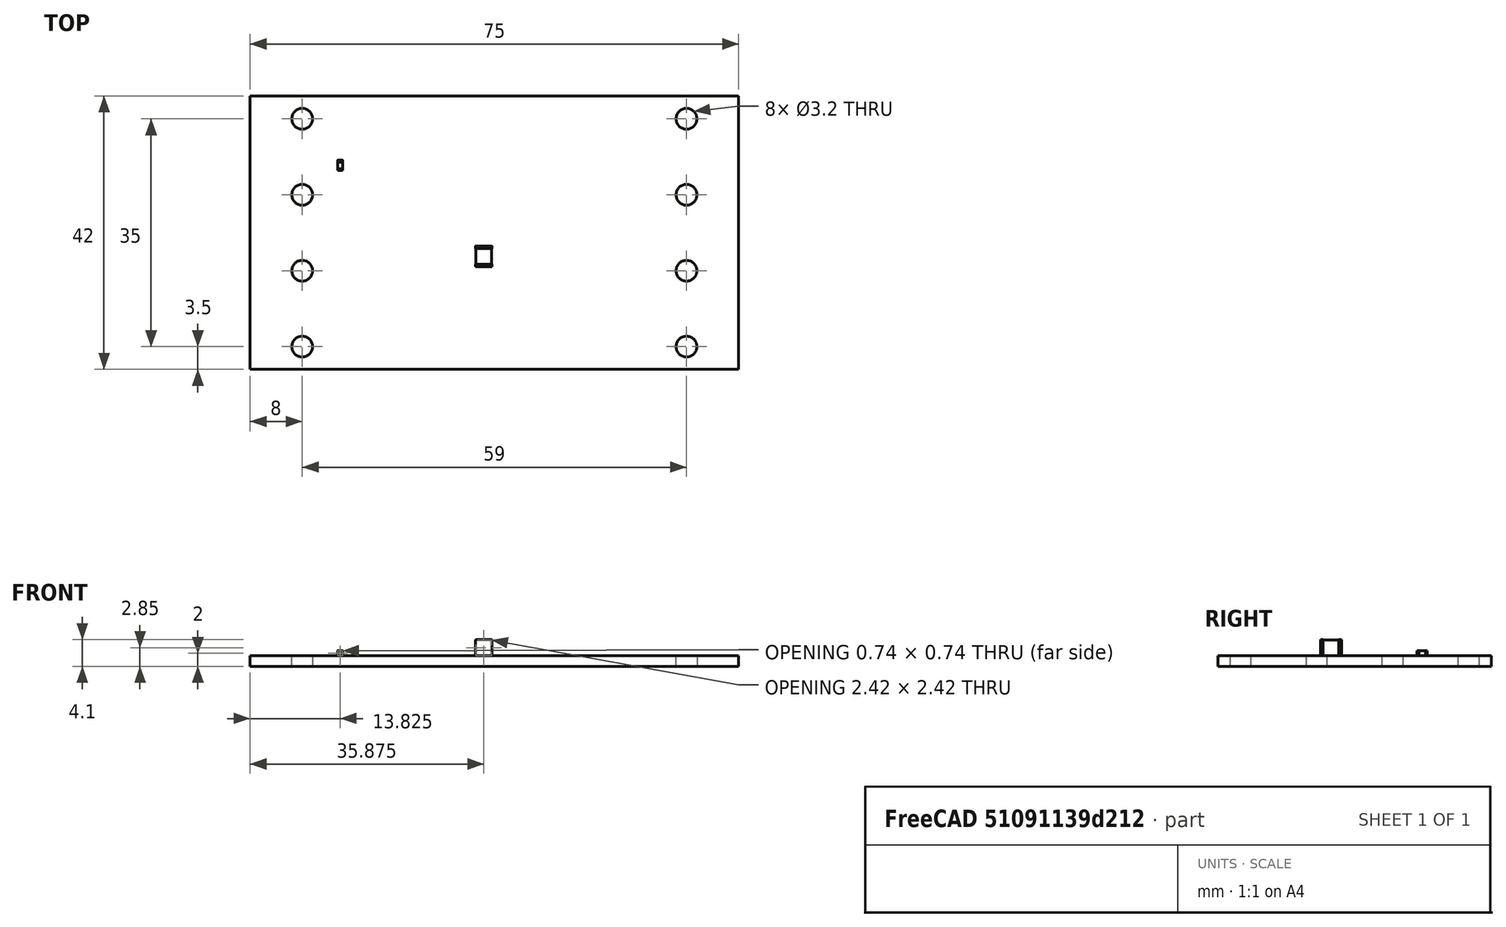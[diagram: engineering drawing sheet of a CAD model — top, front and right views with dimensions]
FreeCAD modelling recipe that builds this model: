
FCSTD DOCUMENT  (FreeCAD 0.19R24291 (Git))
Label: caps
License: Creative Commons Attribution-NonCommercial-ShareAlike
LicenseURL: http://creativecommons.org/licenses/by-nc-sa/4.0/
objects: App::Link×106, PartDesign::Line×8, App::LinkGroup×4, Part::Feature×3, PartDesign::CoordinateSystem×2, Sketcher::SketchObject×1, App::Part×1
note: 14 computed .brp shape members not serialized (recipe doc carries the construction recipe); baked Part::Feature solids carry a one-line shape summary decoded from their .brp

FEATURE [PartDesign::CoordinateSystem] Local_CS_1fb6
  AttacherType = Attacher::AttachEngine3D
FEATURE [Part::Feature] Pcb_1fb6
  Placement = pos=(-110.5,80.5,0) rot=(0,0,1;0rad)
  shape: bbox 75 x 42 x 1.6 mm, 14 faces (baked)
FEATURE [Sketcher::SketchObject] PCB_Sketch_1fb6
  FullyConstrained = false
  sketch-geometry (4):
    g0: LineSegment StartX=0 StartY=0 StartZ=0 EndX=75 EndY=0 EndZ=0
    g1: LineSegment StartX=0 StartY=-42 StartZ=0 EndX=0 EndY=0 EndZ=0
    g2: LineSegment StartX=75 StartY=-42 StartZ=0 EndX=0 EndY=-42 EndZ=0
    g3: LineSegment StartX=75 StartY=0 StartZ=0 EndX=75 EndY=-42 EndZ=0
  constraints (4):
    c: Coincident(g1,g2)
    c: Coincident(g0,g1)
    c: Coincident(g2,g3)
    c: Coincident(g0,g3)
FEATURE [App::LinkGroup] Board_Geoms_1fb6
  ElementList = -> [Pcb_1fb6,Local_CS_1fb6,PCB_Sketch_1fb6]
  LinkMode = 0
FEATURE [Part::Feature] Shape  label="C232_C_0603_1608Metric_6077F2BE"
  Placement = pos=(13.825,-10.655,0) rot=(0,0,-1;1.5708rad)
  shape: bbox 0.8 x 1.6 x 0.8 mm, 28 faces (baked)
FEATURE [App::Link] C232_C_0603_1608Metric_6077F2BE_ln_  label="C231_C_0603_1608Metric_607530A9"
  LinkPlacement = pos=(12.3,-10.65,0) rot=(0,0,-1;1.5708rad)
  LinkedObject = -> Shape
  Placement = pos=(12.3,-10.65,0) rot=(0,0,-1;1.5708rad)
FEATURE [Part::Feature] Shape001  label="C230_C_1210_3225Metric_6077E91F"
  Placement = pos=(35.875,-24.645,0) rot=(0,0,-1;1.5708rad)
  shape: bbox 2.5 x 3.2 x 2.5 mm, 28 faces (baked)
FEATURE [App::Link] C230_C_1210_3225Metric_6077E91F_ln_  label="C229_C_1210_3225Metric_6077F675"
  LinkPlacement = pos=(19.575,-10.655,0) rot=(0,0,-1;1.5708rad)
  LinkedObject = -> Shape001
  Placement = pos=(19.575,-10.655,0) rot=(0,0,-1;1.5708rad)
FEATURE [App::Link] C230_C_1210_3225Metric_6077E91F_ln_001  label="C228_C_1210_3225Metric_6077E3C7"
  LinkPlacement = pos=(32.625,-24.645,0) rot=(0,0,-1;1.5708rad)
  LinkedObject = -> Shape001
  Placement = pos=(32.625,-24.645,0) rot=(0,0,-1;1.5708rad)
FEATURE [App::Link] C230_C_1210_3225Metric_6077E91F_ln_002  label="C227_C_1210_3225Metric_6077FA4A"
  LinkPlacement = pos=(32.575,-10.655,0) rot=(0,0,-1;1.5708rad)
  LinkedObject = -> Shape001
  Placement = pos=(32.575,-10.655,0) rot=(0,0,-1;1.5708rad)
FEATURE [App::Link] C230_C_1210_3225Metric_6077E91F_ln_003  label="C225_C_1210_3225Metric_6077EF6A"
  LinkPlacement = pos=(26.075,-10.655,0) rot=(0,0,-1;1.5708rad)
  LinkedObject = -> Shape001
  Placement = pos=(26.075,-10.655,0) rot=(0,0,-1;1.5708rad)
FEATURE [App::Link] C230_C_1210_3225Metric_6077E91F_ln_004  label="C222_C_1210_3225Metric_6077F4A1"
  LinkPlacement = pos=(26.125,-24.645,0) rot=(0,0,-1;1.5708rad)
  LinkedObject = -> Shape001
  Placement = pos=(26.125,-24.645,0) rot=(0,0,-1;1.5708rad)
FEATURE [App::Link] C230_C_1210_3225Metric_6077E91F_ln_005  label="C221_C_1210_3225Metric_6077EDA8"
  LinkPlacement = pos=(42.325,-10.655,0) rot=(0,0,-1;1.5708rad)
  LinkedObject = -> Shape001
  Placement = pos=(42.325,-10.655,0) rot=(0,0,-1;1.5708rad)
FEATURE [App::Link] C230_C_1210_3225Metric_6077E91F_ln_006  label="C218_C_1210_3225Metric_6077F705"
  LinkPlacement = pos=(16.375,-24.65,0) rot=(0,0,-1;1.5708rad)
  LinkedObject = -> Shape001
  Placement = pos=(16.375,-24.65,0) rot=(0,0,-1;1.5708rad)
FEATURE [App::Link] C230_C_1210_3225Metric_6077E91F_ln_007  label="C217_C_1210_3225Metric_6077EF34"
  LinkPlacement = pos=(16.375,-10.65,0) rot=(0,0,-1;1.5708rad)
  LinkedObject = -> Shape001
  Placement = pos=(16.375,-10.65,0) rot=(0,0,-1;1.5708rad)
FEATURE [App::Link] C230_C_1210_3225Metric_6077E91F_ln_008  label="C216_C_1210_3225Metric_6077F9F0"
  LinkPlacement = pos=(35.825,-10.655,0) rot=(0,0,-1;1.5708rad)
  LinkedObject = -> Shape001
  Placement = pos=(35.825,-10.655,0) rot=(0,0,-1;1.5708rad)
FEATURE [App::Link] C230_C_1210_3225Metric_6077E91F_ln_009  label="C215_C_1210_3225Metric_6077E9EE"
  LinkPlacement = pos=(39.075,-10.655,0) rot=(0,0,-1;1.5708rad)
  LinkedObject = -> Shape001
  Placement = pos=(39.075,-10.655,0) rot=(0,0,-1;1.5708rad)
FEATURE [App::Link] C230_C_1210_3225Metric_6077E91F_ln_010  label="C214_C_1210_3225Metric_6077F0CC"
  LinkPlacement = pos=(19.625,-24.645,0) rot=(0,0,-1;1.5708rad)
  LinkedObject = -> Shape001
  Placement = pos=(19.625,-24.645,0) rot=(0,0,-1;1.5708rad)
FEATURE [App::Link] C230_C_1210_3225Metric_6077E91F_ln_011  label="C213_C_1210_3225Metric_6077EB6E"
  LinkPlacement = pos=(45.625,-24.645,0) rot=(0,0,-1;1.5708rad)
  LinkedObject = -> Shape001
  Placement = pos=(45.625,-24.645,0) rot=(0,0,-1;1.5708rad)
FEATURE [App::Link] C232_C_0603_1608Metric_6077F2BE_ln_001  label="C212_C_0603_1608Metric_6077F138"
  LinkPlacement = pos=(62.625,-24.6325,0) rot=(0,0,-1;1.5708rad)
  LinkedObject = -> Shape
  Placement = pos=(62.625,-24.6325,0) rot=(0,0,-1;1.5708rad)
FEATURE [App::Link] C232_C_0603_1608Metric_6077F2BE_ln_002  label="C211_C_0603_1608Metric_6077E469"
  LinkPlacement = pos=(61.075,-10.655,0) rot=(0,0,-1;1.5708rad)
  LinkedObject = -> Shape
  Placement = pos=(61.075,-10.655,0) rot=(0,0,-1;1.5708rad)
FEATURE [App::Link] C232_C_0603_1608Metric_6077F2BE_ln_003  label="C210_C_0603_1608Metric_6077F9C0"
  LinkPlacement = pos=(12.375,-24.645,0) rot=(0,0,-1;1.5708rad)
  LinkedObject = -> Shape
  Placement = pos=(12.375,-24.645,0) rot=(0,0,-1;1.5708rad)
FEATURE [App::Link] C232_C_0603_1608Metric_6077F2BE_ln_004  label="C209_C_0603_1608Metric_6077E2A4"
  LinkPlacement = pos=(62.575,-10.655,0) rot=(0,0,-1;1.5708rad)
  LinkedObject = -> Shape
  Placement = pos=(62.575,-10.655,0) rot=(0,0,-1;1.5708rad)
FEATURE [App::Link] C230_C_1210_3225Metric_6077E91F_ln_012  label="C208_C_1210_3225Metric_6077F1FE"
  LinkPlacement = pos=(52.075,-10.655,0) rot=(0,0,-1;1.5708rad)
  LinkedObject = -> Shape001
  Placement = pos=(52.075,-10.655,0) rot=(0,0,-1;1.5708rad)
FEATURE [App::Link] C230_C_1210_3225Metric_6077E91F_ln_013  label="C207_C_1210_3225Metric_6077EAE7"
  LinkPlacement = pos=(55.375,-24.645,0) rot=(0,0,-1;1.5708rad)
  LinkedObject = -> Shape001
  Placement = pos=(55.375,-24.645,0) rot=(0,0,-1;1.5708rad)
FEATURE [App::Link] C230_C_1210_3225Metric_6077E91F_ln_014  label="C206_C_1210_3225Metric_6077E7AE"
  LinkPlacement = pos=(48.875,-24.645,0) rot=(0,0,-1;1.5708rad)
  LinkedObject = -> Shape001
  Placement = pos=(48.875,-24.645,0) rot=(0,0,-1;1.5708rad)
FEATURE [App::Link] C230_C_1210_3225Metric_6077E91F_ln_015  label="C204_C_1210_3225Metric_6077EC8B"
  LinkPlacement = pos=(45.575,-10.655,0) rot=(0,0,-1;1.5708rad)
  LinkedObject = -> Shape001
  Placement = pos=(45.575,-10.655,0) rot=(0,0,-1;1.5708rad)
FEATURE [App::Link] C230_C_1210_3225Metric_6077E91F_ln_016  label="C203_C_1210_3225Metric_6077EC58"
  LinkPlacement = pos=(22.875,-24.645,0) rot=(0,0,-1;1.5708rad)
  LinkedObject = -> Shape001
  Placement = pos=(22.875,-24.645,0) rot=(0,0,-1;1.5708rad)
FEATURE [App::Link] C230_C_1210_3225Metric_6077E91F_ln_017  label="C201_C_1210_3225Metric_6077EA1E"
  LinkPlacement = pos=(48.825,-10.655,0) rot=(0,0,-1;1.5708rad)
  LinkedObject = -> Shape001
  Placement = pos=(48.825,-10.655,0) rot=(0,0,-1;1.5708rad)
FEATURE [App::Link] C230_C_1210_3225Metric_6077E91F_ln_018  label="C200_C_1210_3225Metric_6077FC45"
  LinkPlacement = pos=(52.125,-24.645,0) rot=(0,0,-1;1.5708rad)
  LinkedObject = -> Shape001
  Placement = pos=(52.125,-24.645,0) rot=(0,0,-1;1.5708rad)
FEATURE [App::Link] C230_C_1210_3225Metric_6077E91F_ln_019  label="C199_C_1210_3225Metric_6077EAB1"
  LinkPlacement = pos=(55.325,-10.655,0) rot=(0,0,-1;1.5708rad)
  LinkedObject = -> Shape001
  Placement = pos=(55.325,-10.655,0) rot=(0,0,-1;1.5708rad)
FEATURE [App::Link] C230_C_1210_3225Metric_6077E91F_ln_020  label="C198_C_1210_3225Metric_6077F34E"
  LinkPlacement = pos=(29.375,-24.645,0) rot=(0,0,-1;1.5708rad)
  LinkedObject = -> Shape001
  Placement = pos=(29.375,-24.645,0) rot=(0,0,-1;1.5708rad)
FEATURE [App::Link] C230_C_1210_3225Metric_6077E91F_ln_021  label="C196_C_1210_3225Metric_6077EDE1"
  LinkPlacement = pos=(58.625,-24.645,0) rot=(0,0,-1;1.5708rad)
  LinkedObject = -> Shape001
  Placement = pos=(58.625,-24.645,0) rot=(0,0,-1;1.5708rad)
FEATURE [App::Link] C230_C_1210_3225Metric_6077E91F_ln_022  label="C195_C_1210_3225Metric_6077E23E"
  LinkPlacement = pos=(58.575,-10.655,0) rot=(0,0,-1;1.5708rad)
  LinkedObject = -> Shape001
  Placement = pos=(58.575,-10.655,0) rot=(0,0,-1;1.5708rad)
FEATURE [App::Link] C230_C_1210_3225Metric_6077E91F_ln_023  label="C194_C_1210_3225Metric_6077FB79"
  LinkPlacement = pos=(22.825,-10.655,0) rot=(0,0,-1;1.5708rad)
  LinkedObject = -> Shape001
  Placement = pos=(22.825,-10.655,0) rot=(0,0,-1;1.5708rad)
FEATURE [App::Link] C230_C_1210_3225Metric_6077E91F_ln_024  label="C193_C_1210_3225Metric_6077EA7B"
  LinkPlacement = pos=(39.125,-24.645,0) rot=(0,0,-1;1.5708rad)
  LinkedObject = -> Shape001
  Placement = pos=(39.125,-24.645,0) rot=(0,0,-1;1.5708rad)
FEATURE [App::Link] C230_C_1210_3225Metric_6077E91F_ln_025  label="C192_C_1210_3225Metric_6077E5B9"
  LinkPlacement = pos=(42.375,-24.645,0) rot=(0,0,-1;1.5708rad)
  LinkedObject = -> Shape001
  Placement = pos=(42.375,-24.645,0) rot=(0,0,-1;1.5708rad)
FEATURE [App::Link] C230_C_1210_3225Metric_6077E91F_ln_026  label="C191_C_1210_3225Metric_6077E5E9"
  LinkPlacement = pos=(29.325,-10.655,0) rot=(0,0,-1;1.5708rad)
  LinkedObject = -> Shape001
  Placement = pos=(29.325,-10.655,0) rot=(0,0,-1;1.5708rad)
FEATURE [App::Link] C232_C_0603_1608Metric_6077F2BE_ln_005  label="C190_C_0603_1608Metric_6077F465"
  LinkPlacement = pos=(13.875,-24.645,0) rot=(0,0,-1;1.5708rad)
  LinkedObject = -> Shape
  Placement = pos=(13.875,-24.645,0) rot=(0,0,-1;1.5708rad)
FEATURE [App::Link] C232_C_0603_1608Metric_6077F2BE_ln_006  label="C189_C_0603_1608Metric_6077F633"
  LinkPlacement = pos=(61.125,-24.6325,0) rot=(0,0,-1;1.5708rad)
  LinkedObject = -> Shape
  Placement = pos=(61.125,-24.6325,0) rot=(0,0,-1;1.5708rad)
FEATURE [App::Link] C232_C_0603_1608Metric_6077F2BE_ln_007  label="C168_C_0603_1608Metric_6077F7CE"
  LinkPlacement = pos=(12.375,-38.2125,0) rot=(0,0,-1;1.5708rad)
  LinkedObject = -> Shape
  Placement = pos=(12.375,-38.2125,0) rot=(0,0,-1;1.5708rad)
FEATURE [App::Link] C232_C_0603_1608Metric_6077F2BE_ln_008  label="C188_C_0603_1608Metric_6077E1F6"
  LinkPlacement = pos=(62.625,-38.2125,0) rot=(0,0,-1;1.5708rad)
  LinkedObject = -> Shape
  Placement = pos=(62.625,-38.2125,0) rot=(0,0,-1;1.5708rad)
FEATURE [App::Link] C232_C_0603_1608Metric_6077F2BE_ln_009  label="C187_C_0603_1608Metric_6077E391"
  LinkPlacement = pos=(13.875,-38.2125,0) rot=(0,0,-1;1.5708rad)
  LinkedObject = -> Shape
  Placement = pos=(13.875,-38.2125,0) rot=(0,0,-1;1.5708rad)
FEATURE [App::Link] C230_C_1210_3225Metric_6077E91F_ln_027  label="C186_C_1210_3225Metric_6077F381"
  LinkPlacement = pos=(58.625,-38.2125,0) rot=(0,0,-1;1.5708rad)
  LinkedObject = -> Shape001
  Placement = pos=(58.625,-38.2125,0) rot=(0,0,-1;1.5708rad)
FEATURE [App::Link] C230_C_1210_3225Metric_6077E91F_ln_028  label="C184_C_1210_3225Metric_6077F045"
  LinkPlacement = pos=(29.375,-38.2125,0) rot=(0,0,-1;1.5708rad)
  LinkedObject = -> Shape001
  Placement = pos=(29.375,-38.2125,0) rot=(0,0,-1;1.5708rad)
FEATURE [App::Link] C230_C_1210_3225Metric_6077E91F_ln_029  label="C183_C_1210_3225Metric_6077F288"
  LinkPlacement = pos=(16.375,-38.2125,0) rot=(0,0,-1;1.5708rad)
  LinkedObject = -> Shape001
  Placement = pos=(16.375,-38.2125,0) rot=(0,0,-1;1.5708rad)
FEATURE [App::Link] C230_C_1210_3225Metric_6077E91F_ln_030  label="C182_C_1210_3225Metric_6077F906"
  LinkPlacement = pos=(39.125,-38.2125,0) rot=(0,0,-1;1.5708rad)
  LinkedObject = -> Shape001
  Placement = pos=(39.125,-38.2125,0) rot=(0,0,-1;1.5708rad)
FEATURE [App::Link] C230_C_1210_3225Metric_6077E91F_ln_031  label="C180_C_1210_3225Metric_6077F3C3"
  LinkPlacement = pos=(19.625,-38.2125,0) rot=(0,0,-1;1.5708rad)
  LinkedObject = -> Shape001
  Placement = pos=(19.625,-38.2125,0) rot=(0,0,-1;1.5708rad)
FEATURE [App::Link] C230_C_1210_3225Metric_6077E91F_ln_032  label="C179_C_1210_3225Metric_6077E733"
  LinkPlacement = pos=(48.875,-38.2125,0) rot=(0,0,-1;1.5708rad)
  LinkedObject = -> Shape001
  Placement = pos=(48.875,-38.2125,0) rot=(0,0,-1;1.5708rad)
FEATURE [App::Link] C230_C_1210_3225Metric_6077E91F_ln_033  label="C178_C_1210_3225Metric_6077EF9D"
  LinkPlacement = pos=(45.625,-38.2125,0) rot=(0,0,-1;1.5708rad)
  LinkedObject = -> Shape001
  Placement = pos=(45.625,-38.2125,0) rot=(0,0,-1;1.5708rad)
FEATURE [App::Link] C230_C_1210_3225Metric_6077E91F_ln_034  label="C177_C_1210_3225Metric_6077F4EC"
  LinkPlacement = pos=(35.875,-38.2125,0) rot=(0,0,-1;1.5708rad)
  LinkedObject = -> Shape001
  Placement = pos=(35.875,-38.2125,0) rot=(0,0,-1;1.5708rad)
FEATURE [App::Link] C230_C_1210_3225Metric_6077E91F_ln_035  label="C175_C_1210_3225Metric_6077E67C"
  LinkPlacement = pos=(26.125,-38.2125,0) rot=(0,0,-1;1.5708rad)
  LinkedObject = -> Shape001
  Placement = pos=(26.125,-38.2125,0) rot=(0,0,-1;1.5708rad)
FEATURE [App::Link] C230_C_1210_3225Metric_6077E91F_ln_036  label="C174_C_1210_3225Metric_6077FB28"
  LinkPlacement = pos=(52.125,-38.2125,0) rot=(0,0,-1;1.5708rad)
  LinkedObject = -> Shape001
  Placement = pos=(52.125,-38.2125,0) rot=(0,0,-1;1.5708rad)
FEATURE [App::Link] C230_C_1210_3225Metric_6077E91F_ln_037  label="C172_C_1210_3225Metric_6077E61C"
  LinkPlacement = pos=(32.625,-38.2125,0) rot=(0,0,-1;1.5708rad)
  LinkedObject = -> Shape001
  Placement = pos=(32.625,-38.2125,0) rot=(0,0,-1;1.5708rad)
FEATURE [App::Link] C230_C_1210_3225Metric_6077E91F_ln_038  label="C171_C_1210_3225Metric_6077E64C"
  LinkPlacement = pos=(55.375,-38.2125,0) rot=(0,0,-1;1.5708rad)
  LinkedObject = -> Shape001
  Placement = pos=(55.375,-38.2125,0) rot=(0,0,-1;1.5708rad)
FEATURE [App::Link] C230_C_1210_3225Metric_6077E91F_ln_039  label="C170_C_1210_3225Metric_6077F3F3"
  LinkPlacement = pos=(42.375,-38.2125,0) rot=(0,0,-1;1.5708rad)
  LinkedObject = -> Shape001
  Placement = pos=(42.375,-38.2125,0) rot=(0,0,-1;1.5708rad)
FEATURE [App::Link] C230_C_1210_3225Metric_6077E91F_ln_040  label="C169_C_1210_3225Metric_6077F08D"
  LinkPlacement = pos=(22.875,-38.2125,0) rot=(0,0,-1;1.5708rad)
  LinkedObject = -> Shape001
  Placement = pos=(22.875,-38.2125,0) rot=(0,0,-1;1.5708rad)
FEATURE [App::Link] C232_C_0603_1608Metric_6077F2BE_ln_010  label="C167_C_0603_1608Metric_6077F82E"
  LinkPlacement = pos=(61.125,-38.2125,0) rot=(0,0,-1;1.5708rad)
  LinkedObject = -> Shape
  Placement = pos=(61.125,-38.2125,0) rot=(0,0,-1;1.5708rad)
FEATURE [App::Link] C232_C_0603_1608Metric_6077F2BE_ln_011  label="C166_C_0603_1608Metric_6077E982"
  LinkPlacement = pos=(61.125,-31.3125,0) rot=(0,0,-1;1.5708rad)
  LinkedObject = -> Shape
  Placement = pos=(61.125,-31.3125,0) rot=(0,0,-1;1.5708rad)
FEATURE [App::Link] C232_C_0603_1608Metric_6077F2BE_ln_012  label="C165_C_0603_1608Metric_6077ED2D"
  LinkPlacement = pos=(12.375,-31.3125,0) rot=(0,0,-1;1.5708rad)
  LinkedObject = -> Shape
  Placement = pos=(12.375,-31.3125,0) rot=(0,0,-1;1.5708rad)
FEATURE [App::Link] C230_C_1210_3225Metric_6077E91F_ln_041  label="C164_C_1210_3225Metric_6077ED6F"
  LinkPlacement = pos=(16.375,-31.3125,0) rot=(0,0,-1;1.5708rad)
  LinkedObject = -> Shape001
  Placement = pos=(16.375,-31.3125,0) rot=(0,0,-1;1.5708rad)
FEATURE [App::Link] C230_C_1210_3225Metric_6077E91F_ln_042  label="C162_C_1210_3225Metric_6077EE9B"
  LinkPlacement = pos=(19.625,-31.3125,0) rot=(0,0,-1;1.5708rad)
  LinkedObject = -> Shape001
  Placement = pos=(19.625,-31.3125,0) rot=(0,0,-1;1.5708rad)
FEATURE [App::Link] C230_C_1210_3225Metric_6077E91F_ln_043  label="C161_C_1210_3225Metric_6077FA89"
  LinkPlacement = pos=(22.875,-31.3125,0) rot=(0,0,-1;1.5708rad)
  LinkedObject = -> Shape001
  Placement = pos=(22.875,-31.3125,0) rot=(0,0,-1;1.5708rad)
FEATURE [App::Link] C230_C_1210_3225Metric_6077E91F_ln_044  label="C160_C_1210_3225Metric_6077E826"
  LinkPlacement = pos=(35.875,-31.3125,0) rot=(0,0,-1;1.5708rad)
  LinkedObject = -> Shape001
  Placement = pos=(35.875,-31.3125,0) rot=(0,0,-1;1.5708rad)
FEATURE [App::Link] C230_C_1210_3225Metric_6077E91F_ln_045  label="C159_C_1210_3225Metric_6077EBB9"
  LinkPlacement = pos=(26.125,-31.3125,0) rot=(0,0,-1;1.5708rad)
  LinkedObject = -> Shape001
  Placement = pos=(26.125,-31.3125,0) rot=(0,0,-1;1.5708rad)
FEATURE [App::Link] C230_C_1210_3225Metric_6077E91F_ln_046  label="C157_C_1210_3225Metric_6077F23A"
  LinkPlacement = pos=(58.625,-31.3125,0) rot=(0,0,-1;1.5708rad)
  LinkedObject = -> Shape001
  Placement = pos=(58.625,-31.3125,0) rot=(0,0,-1;1.5708rad)
FEATURE [App::Link] C230_C_1210_3225Metric_6077E91F_ln_047  label="C156_C_1210_3225Metric_6077E868"
  LinkPlacement = pos=(42.375,-31.3125,0) rot=(0,0,-1;1.5708rad)
  LinkedObject = -> Shape001
  Placement = pos=(42.375,-31.3125,0) rot=(0,0,-1;1.5708rad)
FEATURE [App::Link] C230_C_1210_3225Metric_6077E91F_ln_048  label="C155_C_1210_3225Metric_6077FCF3"
  LinkPlacement = pos=(29.375,-31.3125,0) rot=(0,0,-1;1.5708rad)
  LinkedObject = -> Shape001
  Placement = pos=(29.375,-31.3125,0) rot=(0,0,-1;1.5708rad)
FEATURE [App::Link] C230_C_1210_3225Metric_6077E91F_ln_049  label="C153_C_1210_3225Metric_6077E9BE"
  LinkPlacement = pos=(48.875,-31.3125,0) rot=(0,0,-1;1.5708rad)
  LinkedObject = -> Shape001
  Placement = pos=(48.875,-31.3125,0) rot=(0,0,-1;1.5708rad)
FEATURE [App::Link] C230_C_1210_3225Metric_6077E91F_ln_050  label="C152_C_1210_3225Metric_6077E26E"
  LinkPlacement = pos=(32.625,-31.3125,0) rot=(0,0,-1;1.5708rad)
  LinkedObject = -> Shape001
  Placement = pos=(32.625,-31.3125,0) rot=(0,0,-1;1.5708rad)
FEATURE [App::Link] C230_C_1210_3225Metric_6077E91F_ln_051  label="C151_C_1210_3225Metric_6077ECFD"
  LinkPlacement = pos=(39.125,-31.3125,0) rot=(0,0,-1;1.5708rad)
  LinkedObject = -> Shape001
  Placement = pos=(39.125,-31.3125,0) rot=(0,0,-1;1.5708rad)
FEATURE [App::Link] C230_C_1210_3225Metric_6077E91F_ln_052  label="C150_C_1210_3225Metric_6077E89B"
  LinkPlacement = pos=(52.125,-31.3125,0) rot=(0,0,-1;1.5708rad)
  LinkedObject = -> Shape001
  Placement = pos=(52.125,-31.3125,0) rot=(0,0,-1;1.5708rad)
FEATURE [App::Link] C230_C_1210_3225Metric_6077E91F_ln_053  label="C149_C_1210_3225Metric_6077F6A5"
  LinkPlacement = pos=(45.625,-31.3125,0) rot=(0,0,-1;1.5708rad)
  LinkedObject = -> Shape001
  Placement = pos=(45.625,-31.3125,0) rot=(0,0,-1;1.5708rad)
FEATURE [App::Link] C230_C_1210_3225Metric_6077E91F_ln_054  label="C148_C_1210_3225Metric_6077E34C"
  LinkPlacement = pos=(55.375,-31.3125,0) rot=(0,0,-1;1.5708rad)
  LinkedObject = -> Shape001
  Placement = pos=(55.375,-31.3125,0) rot=(0,0,-1;1.5708rad)
FEATURE [App::Link] C232_C_0603_1608Metric_6077F2BE_ln_013  label="C146_C_0603_1608Metric_6077E3FA"
  LinkPlacement = pos=(62.625,-31.3125,0) rot=(0,0,-1;1.5708rad)
  LinkedObject = -> Shape
  Placement = pos=(62.625,-31.3125,0) rot=(0,0,-1;1.5708rad)
FEATURE [App::Link] C232_C_0603_1608Metric_6077F2BE_ln_014  label="C145_C_0603_1608Metric_6077ECCA"
  LinkPlacement = pos=(13.875,-31.3125,0) rot=(0,0,-1;1.5708rad)
  LinkedObject = -> Shape
  Placement = pos=(13.875,-31.3125,0) rot=(0,0,-1;1.5708rad)
FEATURE [App::Link] C232_C_0603_1608Metric_6077F2BE_ln_015  label="C144_C_0603_1608Metric_6077E2DD"
  LinkPlacement = pos=(12.375,-17.65,0) rot=(0,0,-1;1.5708rad)
  LinkedObject = -> Shape
  Placement = pos=(12.375,-17.65,0) rot=(0,0,-1;1.5708rad)
FEATURE [App::Link] C232_C_0603_1608Metric_6077F2BE_ln_016  label="C143_C_0603_1608Metric_6077E439"
  LinkPlacement = pos=(13.875,-17.65,0) rot=(0,0,-1;1.5708rad)
  LinkedObject = -> Shape
  Placement = pos=(13.875,-17.65,0) rot=(0,0,-1;1.5708rad)
FEATURE [App::Link] C230_C_1210_3225Metric_6077E91F_ln_055  label="C142_C_1210_3225Metric_6077E4F6"
  LinkPlacement = pos=(52.125,-17.65,0) rot=(0,0,-1;1.5708rad)
  LinkedObject = -> Shape001
  Placement = pos=(52.125,-17.65,0) rot=(0,0,-1;1.5708rad)
FEATURE [App::Link] C230_C_1210_3225Metric_6077E91F_ln_056  label="C141_C_1210_3225Metric_6077FC78"
  LinkPlacement = pos=(35.875,-17.65,0) rot=(0,0,-1;1.5708rad)
  LinkedObject = -> Shape001
  Placement = pos=(35.875,-17.65,0) rot=(0,0,-1;1.5708rad)
FEATURE [App::Link] C230_C_1210_3225Metric_6077E91F_ln_057  label="C140_C_1210_3225Metric_6077F76E"
  LinkPlacement = pos=(22.875,-17.65,0) rot=(0,0,-1;1.5708rad)
  LinkedObject = -> Shape001
  Placement = pos=(22.875,-17.65,0) rot=(0,0,-1;1.5708rad)
FEATURE [App::Link] C230_C_1210_3225Metric_6077E91F_ln_058  label="C139_C_1210_3225Metric_6077F891"
  LinkPlacement = pos=(55.375,-17.65,0) rot=(0,0,-1;1.5708rad)
  LinkedObject = -> Shape001
  Placement = pos=(55.375,-17.65,0) rot=(0,0,-1;1.5708rad)
FEATURE [App::Link] C230_C_1210_3225Metric_6077E91F_ln_059  label="C138_C_1210_3225Metric_6077F423"
  LinkPlacement = pos=(42.375,-17.65,0) rot=(0,0,-1;1.5708rad)
  LinkedObject = -> Shape001
  Placement = pos=(42.375,-17.65,0) rot=(0,0,-1;1.5708rad)
FEATURE [App::Link] C230_C_1210_3225Metric_6077E91F_ln_060  label="C137_C_1210_3225Metric_6077FBAC"
  LinkPlacement = pos=(29.375,-17.65,0) rot=(0,0,-1;1.5708rad)
  LinkedObject = -> Shape001
  Placement = pos=(29.375,-17.65,0) rot=(0,0,-1;1.5708rad)
FEATURE [App::Link] C230_C_1210_3225Metric_6077E91F_ln_061  label="C135_C_1210_3225Metric_6077F16B"
  LinkPlacement = pos=(58.625,-17.65,0) rot=(0,0,-1;1.5708rad)
  LinkedObject = -> Shape001
  Placement = pos=(58.625,-17.65,0) rot=(0,0,-1;1.5708rad)
FEATURE [App::Link] C230_C_1210_3225Metric_6077E91F_ln_062  label="C134_C_1210_3225Metric_6077E76F"
  LinkPlacement = pos=(48.875,-17.65,0) rot=(0,0,-1;1.5708rad)
  LinkedObject = -> Shape001
  Placement = pos=(48.875,-17.65,0) rot=(0,0,-1;1.5708rad)
FEATURE [App::Link] C230_C_1210_3225Metric_6077E91F_ln_063  label="C131_C_1210_3225Metric_6077F5A3"
  LinkPlacement = pos=(19.625,-17.65,0) rot=(0,0,-1;1.5708rad)
  LinkedObject = -> Shape001
  Placement = pos=(19.625,-17.65,0) rot=(0,0,-1;1.5708rad)
FEATURE [App::Link] C230_C_1210_3225Metric_6077E91F_ln_064  label="C129_C_1210_3225Metric_6077F73B"
  LinkPlacement = pos=(39.125,-17.65,0) rot=(0,0,-1;1.5708rad)
  LinkedObject = -> Shape001
  Placement = pos=(39.125,-17.65,0) rot=(0,0,-1;1.5708rad)
FEATURE [App::Link] C230_C_1210_3225Metric_6077E91F_ln_065  label="C128_C_1210_3225Metric_6077F7FE"
  LinkPlacement = pos=(26.125,-17.65,0) rot=(0,0,-1;1.5708rad)
  LinkedObject = -> Shape001
  Placement = pos=(26.125,-17.65,0) rot=(0,0,-1;1.5708rad)
FEATURE [App::Link] C230_C_1210_3225Metric_6077E91F_ln_066  label="C127_C_1210_3225Metric_6077F009"
  LinkPlacement = pos=(45.625,-17.65,0) rot=(0,0,-1;1.5708rad)
  LinkedObject = -> Shape001
  Placement = pos=(45.625,-17.65,0) rot=(0,0,-1;1.5708rad)
FEATURE [App::Link] C230_C_1210_3225Metric_6077E91F_ln_067  label="C126_C_1210_3225Metric_6077F603"
  LinkPlacement = pos=(32.625,-17.65,0) rot=(0,0,-1;1.5708rad)
  LinkedObject = -> Shape001
  Placement = pos=(32.625,-17.65,0) rot=(0,0,-1;1.5708rad)
FEATURE [App::Link] C230_C_1210_3225Metric_6077E91F_ln_068  label="C125_C_1210_3225Metric_6077F31E"
  LinkPlacement = pos=(16.375,-17.65,0) rot=(0,0,-1;1.5708rad)
  LinkedObject = -> Shape001
  Placement = pos=(16.375,-17.65,0) rot=(0,0,-1;1.5708rad)
FEATURE [App::Link] C232_C_0603_1608Metric_6077F2BE_ln_017  label="C124_C_0603_1608Metric_6077F1AA"
  LinkPlacement = pos=(61.125,-17.65,0) rot=(0,0,-1;1.5708rad)
  LinkedObject = -> Shape
  Placement = pos=(61.125,-17.65,0) rot=(0,0,-1;1.5708rad)
FEATURE [App::Link] C232_C_0603_1608Metric_6077F2BE_ln_018  label="C123_C_0603_1608Metric_6077F531"
  LinkPlacement = pos=(62.625,-17.65,0) rot=(0,0,-1;1.5708rad)
  LinkedObject = -> Shape
  Placement = pos=(62.625,-17.65,0) rot=(0,0,-1;1.5708rad)
FEATURE [App::Link] C232_C_0603_1608Metric_6077F2BE_ln_019  label="C122_C_0603_1608Metric_6077F2EE"
  LinkPlacement = pos=(12.375,-3.9,0) rot=(0,0,-1;1.5708rad)
  LinkedObject = -> Shape
  Placement = pos=(12.375,-3.9,0) rot=(0,0,-1;1.5708rad)
FEATURE [App::Link] C232_C_0603_1608Metric_6077F2BE_ln_020  label="C121_C_0603_1608Metric_6077F85E"
  LinkPlacement = pos=(13.875,-3.9,0) rot=(0,0,-1;1.5708rad)
  LinkedObject = -> Shape
  Placement = pos=(13.875,-3.9,0) rot=(0,0,-1;1.5708rad)
FEATURE [App::Link] C230_C_1210_3225Metric_6077E91F_ln_069  label="C120_C_1210_3225Metric_6077F945"
  LinkPlacement = pos=(16.375,-3.9,0) rot=(0,0,-1;1.5708rad)
  LinkedObject = -> Shape001
  Placement = pos=(16.375,-3.9,0) rot=(0,0,-1;1.5708rad)
FEATURE [App::Link] C230_C_1210_3225Metric_6077E91F_ln_070  label="C119_C_1210_3225Metric_6077E52C"
  LinkPlacement = pos=(19.625,-3.9,0) rot=(0,0,-1;1.5708rad)
  LinkedObject = -> Shape001
  Placement = pos=(19.625,-3.9,0) rot=(0,0,-1;1.5708rad)
FEATURE [App::Link] C230_C_1210_3225Metric_6077E91F_ln_071  label="C118_C_1210_3225Metric_6077E4B4"
  LinkPlacement = pos=(22.875,-3.9,0) rot=(0,0,-1;1.5708rad)
  LinkedObject = -> Shape001
  Placement = pos=(22.875,-3.9,0) rot=(0,0,-1;1.5708rad)
FEATURE [App::Link] C230_C_1210_3225Metric_6077E91F_ln_072  label="C117_C_1210_3225Metric_6077F97B"
  LinkPlacement = pos=(26.125,-3.9,0) rot=(0,0,-1;1.5708rad)
  LinkedObject = -> Shape001
  Placement = pos=(26.125,-3.9,0) rot=(0,0,-1;1.5708rad)
FEATURE [App::Link] C230_C_1210_3225Metric_6077E91F_ln_073  label="C116_C_1210_3225Metric_6077E6C1"
  LinkPlacement = pos=(29.375,-3.9,0) rot=(0,0,-1;1.5708rad)
  LinkedObject = -> Shape001
  Placement = pos=(29.375,-3.9,0) rot=(0,0,-1;1.5708rad)
FEATURE [App::Link] C230_C_1210_3225Metric_6077E91F_ln_074  label="C115_C_1210_3225Metric_6077F5D3"
  LinkPlacement = pos=(32.625,-3.9,0) rot=(0,0,-1;1.5708rad)
  LinkedObject = -> Shape001
  Placement = pos=(32.625,-3.9,0) rot=(0,0,-1;1.5708rad)
FEATURE [App::Link] C230_C_1210_3225Metric_6077E91F_ln_075  label="C110_C_1210_3225Metric_6077E1C6"
  LinkPlacement = pos=(35.875,-3.9,0) rot=(0,0,-1;1.5708rad)
  LinkedObject = -> Shape001
  Placement = pos=(35.875,-3.9,0) rot=(0,0,-1;1.5708rad)
FEATURE [App::Link] C230_C_1210_3225Metric_6077E91F_ln_076  label="C109_C_1210_3225Metric_6077E571"
  LinkPlacement = pos=(39.125,-3.9,0) rot=(0,0,-1;1.5708rad)
  LinkedObject = -> Shape001
  Placement = pos=(39.125,-3.9,0) rot=(0,0,-1;1.5708rad)
FEATURE [App::Link] C230_C_1210_3225Metric_6077E91F_ln_077  label="C108_C_1210_3225Metric_6077FCC3"
  LinkPlacement = pos=(42.375,-3.9,0) rot=(0,0,-1;1.5708rad)
  LinkedObject = -> Shape001
  Placement = pos=(42.375,-3.9,0) rot=(0,0,-1;1.5708rad)
FEATURE [App::Link] C230_C_1210_3225Metric_6077E91F_ln_078  label="C107_C_1210_3225Metric_6077EC19"
  LinkPlacement = pos=(45.625,-3.9,0) rot=(0,0,-1;1.5708rad)
  LinkedObject = -> Shape001
  Placement = pos=(45.625,-3.9,0) rot=(0,0,-1;1.5708rad)
FEATURE [App::Link] C230_C_1210_3225Metric_6077E91F_ln_079  label="C106_C_1210_3225Metric_6077EE62"
  LinkPlacement = pos=(48.875,-3.9,0) rot=(0,0,-1;1.5708rad)
  LinkedObject = -> Shape001
  Placement = pos=(48.875,-3.9,0) rot=(0,0,-1;1.5708rad)
FEATURE [App::Link] C230_C_1210_3225Metric_6077E91F_ln_080  label="C105_C_1210_3225Metric_6077F108"
  LinkPlacement = pos=(52.125,-3.9,0) rot=(0,0,-1;1.5708rad)
  LinkedObject = -> Shape001
  Placement = pos=(52.125,-3.9,0) rot=(0,0,-1;1.5708rad)
FEATURE [App::Link] C230_C_1210_3225Metric_6077E91F_ln_081  label="C104_C_1210_3225Metric_6077FAD7"
  LinkPlacement = pos=(55.375,-3.9,0) rot=(0,0,-1;1.5708rad)
  LinkedObject = -> Shape001
  Placement = pos=(55.375,-3.9,0) rot=(0,0,-1;1.5708rad)
FEATURE [App::Link] C230_C_1210_3225Metric_6077E91F_ln_082  label="C103_C_1210_3225Metric_6077EB1A"
  LinkPlacement = pos=(58.625,-3.9,0) rot=(0,0,-1;1.5708rad)
  LinkedObject = -> Shape001
  Placement = pos=(58.625,-3.9,0) rot=(0,0,-1;1.5708rad)
FEATURE [App::Link] C232_C_0603_1608Metric_6077F2BE_ln_021  label="C102_C_0603_1608Metric_6077EE2F"
  LinkPlacement = pos=(62.625,-3.9,0) rot=(0,0,-1;1.5708rad)
  LinkedObject = -> Shape
  Placement = pos=(62.625,-3.9,0) rot=(0,0,-1;1.5708rad)
FEATURE [App::Link] C232_C_0603_1608Metric_6077F2BE_ln_022  label="C101_C_0603_1608Metric_6077F8CA"
  LinkPlacement = pos=(61.125,-3.9,0) rot=(0,0,-1;1.5708rad)
  LinkedObject = -> Shape
  Placement = pos=(61.125,-3.9,0) rot=(0,0,-1;1.5708rad)
FEATURE [App::LinkGroup] Top_1fb6
  ElementList = -> [Shape,C232_C_0603_1608Metric_6077F2BE_ln_,Shape001,C230_C_1210_3225Metric_6077E91F_ln_,C230_C_1210_3225Metric_6077E91F_ln_001,C230_C_1210_3225Metric_6077E91F_ln_002,C230_C_1210_3225Metric_6077E91F_ln_003,C230_C_1210_3225Metric_6077E91F_ln_004,C230_C_1210_3225Metric_6077E91F_ln_005,C230_C_1210_3225Metric_6077E91F_ln_006,C230_C_1210_3225Metric_6077E91F_ln_007,C230_C_1210_3225Metric_6077E91F_ln_008,+96 more]
  LinkMode = 0
FEATURE [App::LinkGroup] Step_Models_1fb6
  ElementList = -> [Top_1fb6]
  LinkMode = 0
FEATURE [App::LinkGroup] Board_1fb6  label="Caps"
  ElementList = -> [Board_Geoms_1fb6,Step_Models_1fb6]
  LinkMode = 0
FEATURE [PartDesign::CoordinateSystem] LCS_0
  AttacherType = Attacher::AttachEngine3D
  MapMode = 2
  Support = -> [X_Axis]
FEATURE [PartDesign::Line] HoleAxis_1
  AttacherType = Attacher::AttachEngineLine
  Length = 4.50902
  MapMode = 19
  Placement = pos=(67,-38.5,0) rot=(0,0,1;0rad)
  ResizeMode = 1
  Support = -> [Pcb_1fb6]
FEATURE [PartDesign::Line] HoleAxis_2
  AttacherType = Attacher::AttachEngineLine
  Length = 4.50902
  MapMode = 19
  Placement = pos=(67,-26.8333,0) rot=(0,0,1;0rad)
  ResizeMode = 1
  Support = -> [Pcb_1fb6]
FEATURE [PartDesign::Line] HoleAxis_3
  AttacherType = Attacher::AttachEngineLine
  Length = 4.50902
  MapMode = 19
  Placement = pos=(67,-15.1667,0) rot=(0,0,1;0rad)
  ResizeMode = 1
  Support = -> [Pcb_1fb6]
FEATURE [PartDesign::Line] HoleAxis_4
  AttacherType = Attacher::AttachEngineLine
  Length = 4.50902
  MapMode = 19
  Placement = pos=(67,-3.5,0) rot=(0,0,1;0rad)
  ResizeMode = 1
  Support = -> [Pcb_1fb6]
FEATURE [PartDesign::Line] HoleAxis_5
  AttacherType = Attacher::AttachEngineLine
  Length = 4.50902
  MapMode = 19
  Placement = pos=(8,-3.5,0) rot=(0,0,1;0rad)
  ResizeMode = 1
  Support = -> [Pcb_1fb6]
FEATURE [PartDesign::Line] HoleAxis_6
  AttacherType = Attacher::AttachEngineLine
  Length = 4.50902
  MapMode = 19
  Placement = pos=(8,-15.1667,0) rot=(0,0,1;0rad)
  ResizeMode = 1
  Support = -> [Pcb_1fb6]
FEATURE [PartDesign::Line] HoleAxis_7
  AttacherType = Attacher::AttachEngineLine
  Length = 4.50902
  MapMode = 19
  Placement = pos=(8,-26.8333,0) rot=(0,0,1;0rad)
  ResizeMode = 1
  Support = -> [Pcb_1fb6]
FEATURE [PartDesign::Line] HoleAxis_8
  AttacherType = Attacher::AttachEngineLine
  Length = 4.50902
  MapMode = 19
  Placement = pos=(8,-38.5,0) rot=(0,0,1;0rad)
  ResizeMode = 1
  Support = -> [Pcb_1fb6]
FEATURE [App::Part] Part
  Group = -> [LCS_0,C230_C_1210_3225Metric_6077E91F_ln_061,C230_C_1210_3225Metric_6077E91F_ln_040,C230_C_1210_3225Metric_6077E91F_ln_068,C230_C_1210_3225Metric_6077E91F_ln_008,C230_C_1210_3225Metric_6077E91F_ln_027,C230_C_1210_3225Metric_6077E91F_ln_072,C232_C_0603_1608Metric_6077F2BE_ln_021,C232_C_0603_1608Metric_6077F2BE_ln_017,C230_C_1210_3225Metric_6077E91F_ln_041,C230_C_1210_3225Metric_6077E91F_ln_052,+113 more]
  Origin = -> Origin
